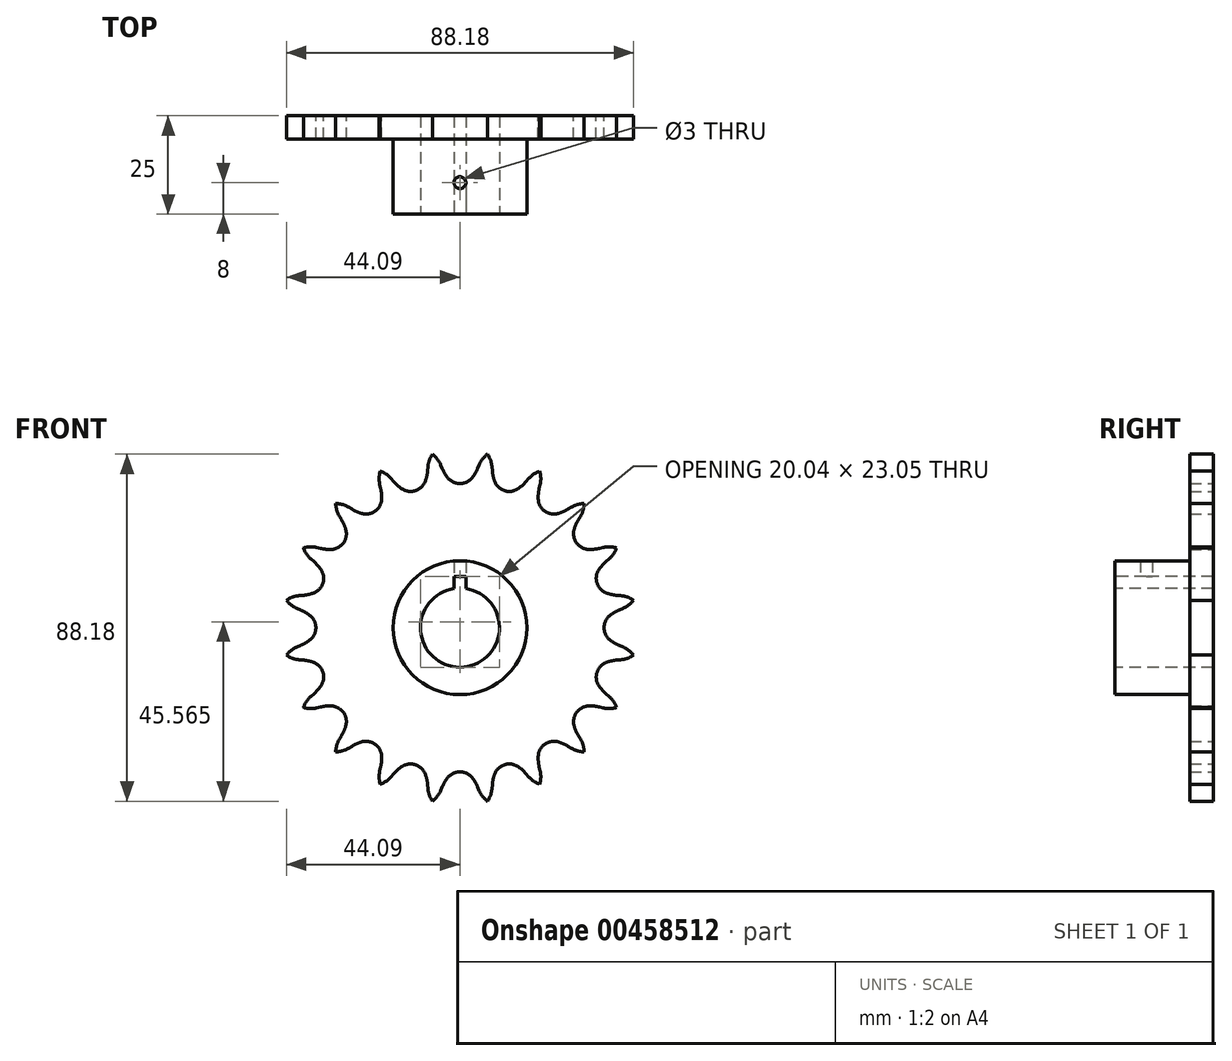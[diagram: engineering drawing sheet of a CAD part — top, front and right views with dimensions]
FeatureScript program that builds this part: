
annotation { "Feature Type Name" : "Feature", "Feature Type Description" : "" }
export const myFeature = defineFeature(function(context is Context, id is Id, definition is map)
    precondition{}
    {
        {
            var Q0;
            Q0=qCreatedBy(makeId("Front.planeOp"),FACE);
            var sketch = newSketch(context, id + "F0", { "sketchPlane" : qUnion([Q0])});
            skCircle(sketch, "E0", {"center": v(0, 0) * mm, "radius": 17 * mm});
            skCircle(sketch, "E1", {"center": v(0, 0) * mm, "radius": 40.6 * mm, "construction": true});
            skLineSegment(sketch, "E2", {"start": v(0, 0) * mm, "end": v(0, 17) * mm, "construction": true});
            skLineSegment(sketch, "E3", {"start": v(-4.52, 40.5) * mm, "end": v(-4.9, 41.4) * mm});
            skArc(sketch, "E4", {"start": v(-4.9, 41.4) * mm, "mid": v(-5.76, 42.88) * mm, "end": v(-6.98, 44.09) * mm});
            skLineSegment(sketch, "E5", {"start": v(0, 0) * mm, "end": v(-2.66, 16.8) * mm, "construction": true});
            skLineSegment(sketch, "E6.trimOffspring", {"start": v(0, 36.61) * mm, "end": v(0, 40.6) * mm, "construction": true});
            skArc(sketch, "E7.trimOffspring", {"start": v(-3.14, 38.14) * mm, "mid": v(-1.75, 37.01) * mm, "end": v(0, 36.61) * mm});
            skArc(sketch, "E8.trimOffspring", {"start": v(-4.52, 40.5) * mm, "mid": v(-3.9, 39.27) * mm, "end": v(-3.14, 38.14) * mm});
            skArc(sketch, "E9.MirrorCS", {"start": v(4.9, 41.4) * mm, "mid": v(5.76, 42.88) * mm, "end": v(6.98, 44.09) * mm});
            skLineSegment(sketch, "E10.MirrorCS", {"start": v(4.52, 40.5) * mm, "end": v(4.9, 41.4) * mm});
            skArc(sketch, "E11.MirrorCS", {"start": v(4.52, 40.5) * mm, "mid": v(3.9, 39.27) * mm, "end": v(3.14, 38.14) * mm});
            skArc(sketch, "E12.MirrorCS", {"start": v(3.14, 38.14) * mm, "mid": v(1.75, 37.01) * mm, "end": v(0, 36.61) * mm});
            skArc(sketch, "E13.1.0", {"start": v(-17.45, 37.86) * mm, "mid": v(-18.73, 39) * mm, "end": v(-20.26, 39.77) * mm});
            skLineSegment(sketch, "E13.1.1", {"start": v(-16.81, 37.12) * mm, "end": v(-17.45, 37.86) * mm});
            skArc(sketch, "E13.1.2", {"start": v(-16.81, 37.12) * mm, "mid": v(-15.85, 36.14) * mm, "end": v(-14.77, 35.3) * mm});
            skArc(sketch, "E13.1.3", {"start": v(-14.77, 35.3) * mm, "mid": v(-13.1, 34.66) * mm, "end": v(-11.31, 34.82) * mm});
            skArc(sketch, "E13.1.4", {"start": v(-8.8, 37.24) * mm, "mid": v(-9.78, 35.74) * mm, "end": v(-11.31, 34.82) * mm});
            skArc(sketch, "E13.1.5", {"start": v(-8.22, 39.9) * mm, "mid": v(-8.42, 38.56) * mm, "end": v(-8.8, 37.24) * mm});
            skLineSegment(sketch, "E13.1.6", {"start": v(-8.22, 39.9) * mm, "end": v(-8.13, 40.89) * mm});
            skArc(sketch, "E13.1.7", {"start": v(-8.13, 40.89) * mm, "mid": v(-7.77, 42.56) * mm, "end": v(-6.98, 44.09) * mm});
            skArc(sketch, "E13.2.0", {"start": v(-28.3, 30.61) * mm, "mid": v(-29.87, 31.3) * mm, "end": v(-31.56, 31.56) * mm});
            skLineSegment(sketch, "E13.2.1", {"start": v(-27.46, 30.1) * mm, "end": v(-28.3, 30.61) * mm});
            skArc(sketch, "E13.2.2", {"start": v(-27.46, 30.1) * mm, "mid": v(-26.24, 29.48) * mm, "end": v(-24.96, 29.01) * mm});
            skArc(sketch, "E13.2.3", {"start": v(-24.96, 29.01) * mm, "mid": v(-23.17, 28.92) * mm, "end": v(-21.52, 29.62) * mm});
            skArc(sketch, "E13.2.4", {"start": v(-19.88, 32.7) * mm, "mid": v(-20.34, 30.97) * mm, "end": v(-21.52, 29.62) * mm});
            skArc(sketch, "E13.2.5", {"start": v(-20.15, 35.42) * mm, "mid": v(-19.92, 34.07) * mm, "end": v(-19.88, 32.7) * mm});
            skLineSegment(sketch, "E13.2.6", {"start": v(-20.15, 35.42) * mm, "end": v(-20.37, 36.37) * mm});
            skArc(sketch, "E13.2.7", {"start": v(-20.37, 36.37) * mm, "mid": v(-20.54, 38.08) * mm, "end": v(-20.26, 39.77) * mm});
            skArc(sketch, "E13.3.0", {"start": v(-36.37, 20.37) * mm, "mid": v(-38.08, 20.54) * mm, "end": v(-39.77, 20.26) * mm});
            skLineSegment(sketch, "E13.3.1", {"start": v(-35.42, 20.15) * mm, "end": v(-36.37, 20.37) * mm});
            skArc(sketch, "E13.3.2", {"start": v(-35.42, 20.15) * mm, "mid": v(-34.07, 19.92) * mm, "end": v(-32.7, 19.88) * mm});
            skArc(sketch, "E13.3.3", {"start": v(-32.7, 19.88) * mm, "mid": v(-30.97, 20.34) * mm, "end": v(-29.62, 21.52) * mm});
            skArc(sketch, "E13.3.4", {"start": v(-29.01, 24.96) * mm, "mid": v(-28.92, 23.17) * mm, "end": v(-29.62, 21.52) * mm});
            skArc(sketch, "E13.3.5", {"start": v(-30.1, 27.46) * mm, "mid": v(-29.48, 26.24) * mm, "end": v(-29.01, 24.96) * mm});
            skLineSegment(sketch, "E13.3.6", {"start": v(-30.1, 27.46) * mm, "end": v(-30.61, 28.3) * mm});
            skArc(sketch, "E13.3.7", {"start": v(-30.61, 28.3) * mm, "mid": v(-31.3, 29.87) * mm, "end": v(-31.56, 31.56) * mm});
            skArc(sketch, "E13.4.0", {"start": v(-40.89, 8.13) * mm, "mid": v(-42.56, 7.77) * mm, "end": v(-44.09, 6.98) * mm});
            skLineSegment(sketch, "E13.4.1", {"start": v(-39.9, 8.22) * mm, "end": v(-40.89, 8.13) * mm});
            skArc(sketch, "E13.4.2", {"start": v(-39.9, 8.22) * mm, "mid": v(-38.56, 8.42) * mm, "end": v(-37.24, 8.8) * mm});
            skArc(sketch, "E13.4.3", {"start": v(-37.24, 8.8) * mm, "mid": v(-35.74, 9.78) * mm, "end": v(-34.82, 11.31) * mm});
            skArc(sketch, "E13.4.4", {"start": v(-35.3, 14.77) * mm, "mid": v(-34.66, 13.1) * mm, "end": v(-34.82, 11.31) * mm});
            skArc(sketch, "E13.4.5", {"start": v(-37.12, 16.81) * mm, "mid": v(-36.14, 15.85) * mm, "end": v(-35.3, 14.77) * mm});
            skLineSegment(sketch, "E13.4.6", {"start": v(-37.12, 16.81) * mm, "end": v(-37.86, 17.45) * mm});
            skArc(sketch, "E13.4.7", {"start": v(-37.86, 17.45) * mm, "mid": v(-39, 18.73) * mm, "end": v(-39.77, 20.26) * mm});
            skArc(sketch, "E13.5.0", {"start": v(-41.4, -4.9) * mm, "mid": v(-42.88, -5.76) * mm, "end": v(-44.09, -6.98) * mm});
            skLineSegment(sketch, "E13.5.1", {"start": v(-40.5, -4.52) * mm, "end": v(-41.4, -4.9) * mm});
            skArc(sketch, "E13.5.2", {"start": v(-40.5, -4.52) * mm, "mid": v(-39.27, -3.9) * mm, "end": v(-38.14, -3.14) * mm});
            skArc(sketch, "E13.5.3", {"start": v(-38.14, -3.14) * mm, "mid": v(-37.01, -1.75) * mm, "end": v(-36.61, 0) * mm});
            skArc(sketch, "E13.5.4", {"start": v(-38.14, 3.14) * mm, "mid": v(-37.01, 1.75) * mm, "end": v(-36.61, 0) * mm});
            skArc(sketch, "E13.5.5", {"start": v(-40.5, 4.52) * mm, "mid": v(-39.27, 3.9) * mm, "end": v(-38.14, 3.14) * mm});
            skLineSegment(sketch, "E13.5.6", {"start": v(-40.5, 4.52) * mm, "end": v(-41.4, 4.9) * mm});
            skArc(sketch, "E13.5.7", {"start": v(-41.4, 4.9) * mm, "mid": v(-42.88, 5.76) * mm, "end": v(-44.09, 6.98) * mm});
            skArc(sketch, "E13.6.0", {"start": v(-37.86, -17.45) * mm, "mid": v(-39, -18.73) * mm, "end": v(-39.77, -20.26) * mm});
            skLineSegment(sketch, "E13.6.1", {"start": v(-37.12, -16.81) * mm, "end": v(-37.86, -17.45) * mm});
            skArc(sketch, "E13.6.2", {"start": v(-37.12, -16.81) * mm, "mid": v(-36.14, -15.85) * mm, "end": v(-35.3, -14.77) * mm});
            skArc(sketch, "E13.6.3", {"start": v(-35.3, -14.77) * mm, "mid": v(-34.66, -13.1) * mm, "end": v(-34.82, -11.31) * mm});
            skArc(sketch, "E13.6.4", {"start": v(-37.24, -8.8) * mm, "mid": v(-35.74, -9.78) * mm, "end": v(-34.82, -11.31) * mm});
            skArc(sketch, "E13.6.5", {"start": v(-39.9, -8.22) * mm, "mid": v(-38.56, -8.42) * mm, "end": v(-37.24, -8.8) * mm});
            skLineSegment(sketch, "E13.6.6", {"start": v(-39.9, -8.22) * mm, "end": v(-40.89, -8.13) * mm});
            skArc(sketch, "E13.6.7", {"start": v(-40.89, -8.13) * mm, "mid": v(-42.56, -7.77) * mm, "end": v(-44.09, -6.98) * mm});
            skArc(sketch, "E13.7.0", {"start": v(-30.61, -28.3) * mm, "mid": v(-31.3, -29.87) * mm, "end": v(-31.56, -31.56) * mm});
            skLineSegment(sketch, "E13.7.1", {"start": v(-30.1, -27.46) * mm, "end": v(-30.61, -28.3) * mm});
            skArc(sketch, "E13.7.2", {"start": v(-30.1, -27.46) * mm, "mid": v(-29.48, -26.24) * mm, "end": v(-29.01, -24.96) * mm});
            skArc(sketch, "E13.7.3", {"start": v(-29.01, -24.96) * mm, "mid": v(-28.92, -23.17) * mm, "end": v(-29.62, -21.52) * mm});
            skArc(sketch, "E13.7.4", {"start": v(-32.7, -19.88) * mm, "mid": v(-30.97, -20.34) * mm, "end": v(-29.62, -21.52) * mm});
            skArc(sketch, "E13.7.5", {"start": v(-35.42, -20.15) * mm, "mid": v(-34.07, -19.92) * mm, "end": v(-32.7, -19.88) * mm});
            skLineSegment(sketch, "E13.7.6", {"start": v(-35.42, -20.15) * mm, "end": v(-36.37, -20.37) * mm});
            skArc(sketch, "E13.7.7", {"start": v(-36.37, -20.37) * mm, "mid": v(-38.08, -20.54) * mm, "end": v(-39.77, -20.26) * mm});
            skArc(sketch, "E13.8.0", {"start": v(-20.37, -36.37) * mm, "mid": v(-20.54, -38.08) * mm, "end": v(-20.26, -39.77) * mm});
            skLineSegment(sketch, "E13.8.1", {"start": v(-20.15, -35.42) * mm, "end": v(-20.37, -36.37) * mm});
            skArc(sketch, "E13.8.2", {"start": v(-20.15, -35.42) * mm, "mid": v(-19.92, -34.07) * mm, "end": v(-19.88, -32.7) * mm});
            skArc(sketch, "E13.8.3", {"start": v(-19.88, -32.7) * mm, "mid": v(-20.34, -30.97) * mm, "end": v(-21.52, -29.62) * mm});
            skArc(sketch, "E13.8.4", {"start": v(-24.96, -29.01) * mm, "mid": v(-23.17, -28.92) * mm, "end": v(-21.52, -29.62) * mm});
            skArc(sketch, "E13.8.5", {"start": v(-27.46, -30.1) * mm, "mid": v(-26.24, -29.48) * mm, "end": v(-24.96, -29.01) * mm});
            skLineSegment(sketch, "E13.8.6", {"start": v(-27.46, -30.1) * mm, "end": v(-28.3, -30.61) * mm});
            skArc(sketch, "E13.8.7", {"start": v(-28.3, -30.61) * mm, "mid": v(-29.87, -31.3) * mm, "end": v(-31.56, -31.56) * mm});
            skArc(sketch, "E13.9.0", {"start": v(-8.13, -40.89) * mm, "mid": v(-7.77, -42.56) * mm, "end": v(-6.98, -44.09) * mm});
            skLineSegment(sketch, "E13.9.1", {"start": v(-8.22, -39.9) * mm, "end": v(-8.13, -40.89) * mm});
            skArc(sketch, "E13.9.2", {"start": v(-8.22, -39.9) * mm, "mid": v(-8.42, -38.56) * mm, "end": v(-8.8, -37.24) * mm});
            skArc(sketch, "E13.9.3", {"start": v(-8.8, -37.24) * mm, "mid": v(-9.78, -35.74) * mm, "end": v(-11.31, -34.82) * mm});
            skArc(sketch, "E13.9.4", {"start": v(-14.77, -35.3) * mm, "mid": v(-13.1, -34.66) * mm, "end": v(-11.31, -34.82) * mm});
            skArc(sketch, "E13.9.5", {"start": v(-16.81, -37.12) * mm, "mid": v(-15.85, -36.14) * mm, "end": v(-14.77, -35.3) * mm});
            skLineSegment(sketch, "E13.9.6", {"start": v(-16.81, -37.12) * mm, "end": v(-17.45, -37.86) * mm});
            skArc(sketch, "E13.9.7", {"start": v(-17.45, -37.86) * mm, "mid": v(-18.73, -39) * mm, "end": v(-20.26, -39.77) * mm});
            skArc(sketch, "E13.10.0", {"start": v(4.9, -41.4) * mm, "mid": v(5.76, -42.88) * mm, "end": v(6.98, -44.09) * mm});
            skLineSegment(sketch, "E13.10.1", {"start": v(4.52, -40.5) * mm, "end": v(4.9, -41.4) * mm});
            skArc(sketch, "E13.10.2", {"start": v(4.52, -40.5) * mm, "mid": v(3.9, -39.27) * mm, "end": v(3.14, -38.14) * mm});
            skArc(sketch, "E13.10.3", {"start": v(3.14, -38.14) * mm, "mid": v(1.75, -37.01) * mm, "end": v(0, -36.61) * mm});
            skArc(sketch, "E13.10.4", {"start": v(-3.14, -38.14) * mm, "mid": v(-1.75, -37.01) * mm, "end": v(0, -36.61) * mm});
            skArc(sketch, "E13.10.5", {"start": v(-4.52, -40.5) * mm, "mid": v(-3.9, -39.27) * mm, "end": v(-3.14, -38.14) * mm});
            skLineSegment(sketch, "E13.10.6", {"start": v(-4.52, -40.5) * mm, "end": v(-4.9, -41.4) * mm});
            skArc(sketch, "E13.10.7", {"start": v(-4.9, -41.4) * mm, "mid": v(-5.76, -42.88) * mm, "end": v(-6.98, -44.09) * mm});
            skArc(sketch, "E13.11.0", {"start": v(17.45, -37.86) * mm, "mid": v(18.73, -39) * mm, "end": v(20.26, -39.77) * mm});
            skLineSegment(sketch, "E13.11.1", {"start": v(16.81, -37.12) * mm, "end": v(17.45, -37.86) * mm});
            skArc(sketch, "E13.11.2", {"start": v(16.81, -37.12) * mm, "mid": v(15.85, -36.14) * mm, "end": v(14.77, -35.3) * mm});
            skArc(sketch, "E13.11.3", {"start": v(14.77, -35.3) * mm, "mid": v(13.1, -34.66) * mm, "end": v(11.31, -34.82) * mm});
            skArc(sketch, "E13.11.4", {"start": v(8.8, -37.24) * mm, "mid": v(9.78, -35.74) * mm, "end": v(11.31, -34.82) * mm});
            skArc(sketch, "E13.11.5", {"start": v(8.22, -39.9) * mm, "mid": v(8.42, -38.56) * mm, "end": v(8.8, -37.24) * mm});
            skLineSegment(sketch, "E13.11.6", {"start": v(8.22, -39.9) * mm, "end": v(8.13, -40.89) * mm});
            skArc(sketch, "E13.11.7", {"start": v(8.13, -40.89) * mm, "mid": v(7.77, -42.56) * mm, "end": v(6.98, -44.09) * mm});
            skArc(sketch, "E13.12.0", {"start": v(28.3, -30.61) * mm, "mid": v(29.87, -31.3) * mm, "end": v(31.56, -31.56) * mm});
            skLineSegment(sketch, "E13.12.1", {"start": v(27.46, -30.1) * mm, "end": v(28.3, -30.61) * mm});
            skArc(sketch, "E13.12.2", {"start": v(27.46, -30.1) * mm, "mid": v(26.24, -29.48) * mm, "end": v(24.96, -29.01) * mm});
            skArc(sketch, "E13.12.3", {"start": v(24.96, -29.01) * mm, "mid": v(23.17, -28.92) * mm, "end": v(21.52, -29.62) * mm});
            skArc(sketch, "E13.12.4", {"start": v(19.88, -32.7) * mm, "mid": v(20.34, -30.97) * mm, "end": v(21.52, -29.62) * mm});
            skArc(sketch, "E13.12.5", {"start": v(20.15, -35.42) * mm, "mid": v(19.92, -34.07) * mm, "end": v(19.88, -32.7) * mm});
            skLineSegment(sketch, "E13.12.6", {"start": v(20.15, -35.42) * mm, "end": v(20.37, -36.37) * mm});
            skArc(sketch, "E13.12.7", {"start": v(20.37, -36.37) * mm, "mid": v(20.54, -38.08) * mm, "end": v(20.26, -39.77) * mm});
            skArc(sketch, "E13.13.0", {"start": v(36.37, -20.37) * mm, "mid": v(38.08, -20.54) * mm, "end": v(39.77, -20.26) * mm});
            skLineSegment(sketch, "E13.13.1", {"start": v(35.42, -20.15) * mm, "end": v(36.37, -20.37) * mm});
            skArc(sketch, "E13.13.2", {"start": v(35.42, -20.15) * mm, "mid": v(34.07, -19.92) * mm, "end": v(32.7, -19.88) * mm});
            skArc(sketch, "E13.13.3", {"start": v(32.7, -19.88) * mm, "mid": v(30.97, -20.34) * mm, "end": v(29.62, -21.52) * mm});
            skArc(sketch, "E13.13.4", {"start": v(29.01, -24.96) * mm, "mid": v(28.92, -23.17) * mm, "end": v(29.62, -21.52) * mm});
            skArc(sketch, "E13.13.5", {"start": v(30.1, -27.46) * mm, "mid": v(29.48, -26.24) * mm, "end": v(29.01, -24.96) * mm});
            skLineSegment(sketch, "E13.13.6", {"start": v(30.1, -27.46) * mm, "end": v(30.61, -28.3) * mm});
            skArc(sketch, "E13.13.7", {"start": v(30.61, -28.3) * mm, "mid": v(31.3, -29.87) * mm, "end": v(31.56, -31.56) * mm});
            skArc(sketch, "E13.14.0", {"start": v(40.89, -8.13) * mm, "mid": v(42.56, -7.77) * mm, "end": v(44.09, -6.98) * mm});
            skLineSegment(sketch, "E13.14.1", {"start": v(39.9, -8.22) * mm, "end": v(40.89, -8.13) * mm});
            skArc(sketch, "E13.14.2", {"start": v(39.9, -8.22) * mm, "mid": v(38.56, -8.42) * mm, "end": v(37.24, -8.8) * mm});
            skArc(sketch, "E13.14.3", {"start": v(37.24, -8.8) * mm, "mid": v(35.74, -9.78) * mm, "end": v(34.82, -11.31) * mm});
            skArc(sketch, "E13.14.4", {"start": v(35.3, -14.77) * mm, "mid": v(34.66, -13.1) * mm, "end": v(34.82, -11.31) * mm});
            skArc(sketch, "E13.14.5", {"start": v(37.12, -16.81) * mm, "mid": v(36.14, -15.85) * mm, "end": v(35.3, -14.77) * mm});
            skLineSegment(sketch, "E13.14.6", {"start": v(37.12, -16.81) * mm, "end": v(37.86, -17.45) * mm});
            skArc(sketch, "E13.14.7", {"start": v(37.86, -17.45) * mm, "mid": v(39, -18.73) * mm, "end": v(39.77, -20.26) * mm});
            skArc(sketch, "E13.15.0", {"start": v(41.4, 4.9) * mm, "mid": v(42.88, 5.76) * mm, "end": v(44.09, 6.98) * mm});
            skLineSegment(sketch, "E13.15.1", {"start": v(40.5, 4.52) * mm, "end": v(41.4, 4.9) * mm});
            skArc(sketch, "E13.15.2", {"start": v(40.5, 4.52) * mm, "mid": v(39.27, 3.9) * mm, "end": v(38.14, 3.14) * mm});
            skArc(sketch, "E13.15.3", {"start": v(38.14, 3.14) * mm, "mid": v(37.01, 1.75) * mm, "end": v(36.61, 0) * mm});
            skArc(sketch, "E13.15.4", {"start": v(38.14, -3.14) * mm, "mid": v(37.01, -1.75) * mm, "end": v(36.61, 0) * mm});
            skArc(sketch, "E13.15.5", {"start": v(40.5, -4.52) * mm, "mid": v(39.27, -3.9) * mm, "end": v(38.14, -3.14) * mm});
            skLineSegment(sketch, "E13.15.6", {"start": v(40.5, -4.52) * mm, "end": v(41.4, -4.9) * mm});
            skArc(sketch, "E13.15.7", {"start": v(41.4, -4.9) * mm, "mid": v(42.88, -5.76) * mm, "end": v(44.09, -6.98) * mm});
            skArc(sketch, "E13.16.0", {"start": v(37.86, 17.45) * mm, "mid": v(39, 18.73) * mm, "end": v(39.77, 20.26) * mm});
            skLineSegment(sketch, "E13.16.1", {"start": v(37.12, 16.81) * mm, "end": v(37.86, 17.45) * mm});
            skArc(sketch, "E13.16.2", {"start": v(37.12, 16.81) * mm, "mid": v(36.14, 15.85) * mm, "end": v(35.3, 14.77) * mm});
            skArc(sketch, "E13.16.3", {"start": v(35.3, 14.77) * mm, "mid": v(34.66, 13.1) * mm, "end": v(34.82, 11.31) * mm});
            skArc(sketch, "E13.16.4", {"start": v(37.24, 8.8) * mm, "mid": v(35.74, 9.78) * mm, "end": v(34.82, 11.31) * mm});
            skArc(sketch, "E13.16.5", {"start": v(39.9, 8.22) * mm, "mid": v(38.56, 8.42) * mm, "end": v(37.24, 8.8) * mm});
            skLineSegment(sketch, "E13.16.6", {"start": v(39.9, 8.22) * mm, "end": v(40.89, 8.13) * mm});
            skArc(sketch, "E13.16.7", {"start": v(40.89, 8.13) * mm, "mid": v(42.56, 7.77) * mm, "end": v(44.09, 6.98) * mm});
            skArc(sketch, "E13.17.0", {"start": v(30.61, 28.3) * mm, "mid": v(31.3, 29.87) * mm, "end": v(31.56, 31.56) * mm});
            skLineSegment(sketch, "E13.17.1", {"start": v(30.1, 27.46) * mm, "end": v(30.61, 28.3) * mm});
            skArc(sketch, "E13.17.2", {"start": v(30.1, 27.46) * mm, "mid": v(29.48, 26.24) * mm, "end": v(29.01, 24.96) * mm});
            skArc(sketch, "E13.17.3", {"start": v(29.01, 24.96) * mm, "mid": v(28.92, 23.17) * mm, "end": v(29.62, 21.52) * mm});
            skArc(sketch, "E13.17.4", {"start": v(32.7, 19.88) * mm, "mid": v(30.97, 20.34) * mm, "end": v(29.62, 21.52) * mm});
            skArc(sketch, "E13.17.5", {"start": v(35.42, 20.15) * mm, "mid": v(34.07, 19.92) * mm, "end": v(32.7, 19.88) * mm});
            skLineSegment(sketch, "E13.17.6", {"start": v(35.42, 20.15) * mm, "end": v(36.37, 20.37) * mm});
            skArc(sketch, "E13.17.7", {"start": v(36.37, 20.37) * mm, "mid": v(38.08, 20.54) * mm, "end": v(39.77, 20.26) * mm});
            skArc(sketch, "E13.18.0", {"start": v(20.37, 36.37) * mm, "mid": v(20.54, 38.08) * mm, "end": v(20.26, 39.77) * mm});
            skLineSegment(sketch, "E13.18.1", {"start": v(20.15, 35.42) * mm, "end": v(20.37, 36.37) * mm});
            skArc(sketch, "E13.18.2", {"start": v(20.15, 35.42) * mm, "mid": v(19.92, 34.07) * mm, "end": v(19.88, 32.7) * mm});
            skArc(sketch, "E13.18.3", {"start": v(19.88, 32.7) * mm, "mid": v(20.34, 30.97) * mm, "end": v(21.52, 29.62) * mm});
            skArc(sketch, "E13.18.4", {"start": v(24.96, 29.01) * mm, "mid": v(23.17, 28.92) * mm, "end": v(21.52, 29.62) * mm});
            skArc(sketch, "E13.18.5", {"start": v(27.46, 30.1) * mm, "mid": v(26.24, 29.48) * mm, "end": v(24.96, 29.01) * mm});
            skLineSegment(sketch, "E13.18.6", {"start": v(27.46, 30.1) * mm, "end": v(28.3, 30.61) * mm});
            skArc(sketch, "E13.18.7", {"start": v(28.3, 30.61) * mm, "mid": v(29.87, 31.3) * mm, "end": v(31.56, 31.56) * mm});
            skArc(sketch, "E13.19.0", {"start": v(8.13, 40.89) * mm, "mid": v(7.77, 42.56) * mm, "end": v(6.98, 44.09) * mm});
            skLineSegment(sketch, "E13.19.1", {"start": v(8.22, 39.9) * mm, "end": v(8.13, 40.89) * mm});
            skArc(sketch, "E13.19.2", {"start": v(8.22, 39.9) * mm, "mid": v(8.42, 38.56) * mm, "end": v(8.8, 37.24) * mm});
            skArc(sketch, "E13.19.3", {"start": v(8.8, 37.24) * mm, "mid": v(9.78, 35.74) * mm, "end": v(11.31, 34.82) * mm});
            skArc(sketch, "E13.19.4", {"start": v(14.77, 35.3) * mm, "mid": v(13.1, 34.66) * mm, "end": v(11.31, 34.82) * mm});
            skArc(sketch, "E13.19.5", {"start": v(16.81, 37.12) * mm, "mid": v(15.85, 36.14) * mm, "end": v(14.77, 35.3) * mm});
            skLineSegment(sketch, "E13.19.6", {"start": v(16.81, 37.12) * mm, "end": v(17.45, 37.86) * mm});
            skArc(sketch, "E13.19.7", {"start": v(17.45, 37.86) * mm, "mid": v(18.73, 39) * mm, "end": v(20.26, 39.77) * mm});
            skSolve(sketch);
        }
        {
            var Q0;
            Q0=makeQuery(id+"F0.imprint","IMPRINT",FACE,{"disambiguationData":[TD([[makeQuery(id+"F0.imprint","IMPRINT",EDGE,{"derivedFrom":sQuery(id+"F0.wireOp",EDGE,"E0")}),1.0]])]});
            extrude(context, id + "F1", {"entities" : qUnion([Q0]), "depth" : 25 * mm, "offsetDistance" : 25 * mm});
        }
        {
            var Q0;
            Q0 = qSketchRegion(id + "F0", true);
            extrude(context, id + "F2", {"entities" : qUnion([Q0]), "operationType" : NewBodyOperationType.ADD, "depth" : 6 * mm, "offsetDistance" : 25 * mm});
        }
        {
            var Q0;
            Q0=makeQuery(id+"F1.opExtrude","CAP_FACE",FACE,{"disambiguationData":[OSD([sQuery(id+"F0.wireOp",EDGE,"E0")])],"isStart":false});
            var sketch = newSketch(context, id + "F3", { "sketchPlane" : qUnion([Q0])});
            skCircle(sketch, "E14", {"center": v(0, 0) * mm, "radius": 10.05 * mm});
            skSolve(sketch);
        }
        {
            var Q0;
            Q0=makeQuery(id+"F3.imprint","IMPRINT",FACE,{"disambiguationData":[TD([[makeQuery(id+"F3.imprint","IMPRINT",EDGE,{"derivedFrom":sQuery(id+"F3.wireOp",EDGE,"E14")}),1.0]])]});
            extrude(context, id + "F4", {"entities" : qUnion([Q0]), "operationType" : NewBodyOperationType.REMOVE, "oppositeDirection" : true, "depth" : 25 * mm, "offsetDistance" : 25 * mm});
        }
        {
            var Q0;
            Q0=makeQuery(id+"F1.opExtrude","CAP_FACE",FACE,{"disambiguationData":[OSD([sQuery(id+"F0.wireOp",EDGE,"E0")])],"isStart":false});
            var sketch = newSketch(context, id + "F5", { "sketchPlane" : qUnion([Q0])});
            skLineSegment(sketch, "E15.bottom", {"start": v(1.5, 0) * mm, "end": v(-1.5, 0) * mm});
            skLineSegment(sketch, "E15.top", {"start": v(1.5, 13) * mm, "end": v(-1.5, 13) * mm});
            skLineSegment(sketch, "E15.left", {"start": v(1.5, 0) * mm, "end": v(1.5, 13) * mm});
            skLineSegment(sketch, "E15.right", {"start": v(-1.5, 0) * mm, "end": v(-1.5, 13) * mm});
            skSolve(sketch);
        }
        {
            var Q0;
            {var subQ0=sQuery(id+"F5.wireOp",EDGE,"E15.top");Q0=makeQuery(id+"F5.imprint","IMPRINT",FACE,{"disambiguationData":[TD([[makeQuery(id+"F5.imprint","IMPRINT",EDGE,{"derivedFrom":subQ0}),1.0]])]});}
            extrude(context, id + "F6", {"entities" : qUnion([Q0]), "operationType" : NewBodyOperationType.REMOVE, "oppositeDirection" : true, "depth" : 25 * mm, "offsetDistance" : 25 * mm});
        }
        {
            var Q0;
            Q0=qCreatedBy(makeId("Top.planeOp"),FACE);
            var sketch = newSketch(context, id + "F7", { "sketchPlane" : qUnion([Q0])});
            skCircle(sketch, "E16", {"center": v(0, -17) * mm, "radius": 1.5 * mm});
            skSolve(sketch);
        }
        {
            var Q0;
            Q0 = qSketchRegion(id + "F7", true);
            extrude(context, id + "F8", {"entities" : qUnion([Q0]), "operationType" : NewBodyOperationType.REMOVE, "depth" : 25 * mm, "offsetDistance" : 25 * mm});
        }
    });
